# Revit family: FalsoTecho_THU_Bandeja-Murano-300
name_source: partatom
category: Modelos genéricos
revit_build: Autodesk Revit 2016 (Build: 20160720_0715(x64)
units: mm (PartAtom-declared; Revit-internal decimal feet)

## family parameters
Compartido = Sí
Corte con vacíos al cargar = Sí
Cota de conector redondo = Diámetro de uso
Puede alojar armadura = No
Punto de cálculo de habitación = No
Se basa en plano de trabajo = Sí
Siempre vertical = No
Tipo de pieza = Normal

## types (1)
- Acero-300xLV
    Bandeja_Espesor = 1 mm  [stored 0.00328084 ft]
    Bandeja_Grosor = 35 mm  [stored 0.114829 ft]
    Bandeja_Separación trans = 0 mm  [stored 0 ft]
    COBie Type Category = L387 : Suspended ceilings
    Comentarios de tipo = Bandejas Techo Murano, para ser montadas en interior de edificios con perfilería THU Murano.
    Declaración de prestaciones = http://thu.es
    Descripción = Bandeja THU de ancho 300 mm y de longitud variable según necesidades (longitud máxima de 2,5 metros) y registrable en cualquier punto. El techo Murano se monta con perfileria oculta THU Murano y rematada perimetralmente sobre angulares de 24 mm. El perfil Murano de 28 mm de ancho y 3,70 m de longitud, fabricado con fleje de acero galvanizado, presenta unas pequeñas alas verticales especialmente diseñadas para el correcto alojamiento de las bandejas Murano.
    Elevación por defecto = 0 mm  [stored 0 ft]
    Fabricante = THU Perfil S.L.
    Famila del producto = Techos metálicos
    Ficha resumen = http://thu.es
    Ficha técnica = http://thu.es
    Grupo del producto = Bandejas
    IFC Classification = IfcCovering (CEILING)
    Manual de montaje = http://thu.es
    Marca = THU
    NBS Reference = 20-10-10/110
    NBS Reference Description = Board suspended ceiling system
    Nombre del objeto = Bandeja Murano 600x600
    Número de edición (versión) = 0
    Omniclass = 23-15 19 23 11
    Perfil secundario_Intereje = 300 mm
    Perfil_Descuelgue = 0 mm  [stored 0 ft]
    Perfiles perimetrales_Desfase altura = 1 mm  [stored 0.00328084 ft]
    Página web del fabricante = http://thu.es
    Página web del producto = http://thu.es
    Solape_Perfil y tirante = 7 mm  [stored 0.0229659 ft]
    THU_Bandeja_Material = Acero
    THU_Reacción al fuego = A2, s1-d0
    THU_Subestructura_Material = Acero galvanizado

note: [stored X ft] marks values corroborated as IEEE doubles in the binary element streams (Revit-internal decimal feet)
